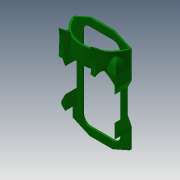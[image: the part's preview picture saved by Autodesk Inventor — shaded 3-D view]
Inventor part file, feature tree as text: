
AUTODESK INVENTOR PART (.ipt)
format: ipt  version: 2013 (Build 170138000, 138)  size: 726,016 bytes
history: native  units: mm
features: sketch x30, extrude x29, chamfer x3, fillet x2
ambient origin geometry x8: Origin, YZ Plane, XZ Plane, XY Plane, X Axis, Y Axis, Z Axis, Center Point
bodies: Solid1 (feature_tree)
feature tree (64):
  extrude  "Extrusion1"  Depth=4.0mm
  extrude  "Extrusion2"  Depth=4.0mm
  extrude  "Extrusion3"  Depth=4.0mm
  fillet  "Fillet1"  Radius=4.0mm
  extrude  "Extrusion4"  Depth=4.0mm
  extrude  "Extrusion5"  Depth=4.0mm
  extrude  "Extrusion6"  Depth=4.0mm
  sketch  "Sketch8"  dims[d13=4.0mm d14=4.0mm]
  extrude  "Extrusion7"  Depth=4.0mm
  extrude  "Extrusion8"  Depth=4.0mm
  extrude  "Extrusion9"  Depth=4.0mm
  extrude  "Extrusion10"  Depth=4.0mm
  extrude  "Extrusion11"  Depth=4.0mm
  extrude  "Extrusion12"  Depth=4.0mm
  extrude  "Extrusion13"  Depth=1.3mm TaperAngle=0.0deg
  extrude  "Extrusion14"  Depth=10.0mm
  extrude  "Extrusion15"  Depth=10.0mm
  extrude  "Extrusion16"  Depth=10.0mm
  extrude  "Extrusion17"  Depth=20.0mm
  extrude  "Extrusion18"  Depth=3.3mm TaperAngle=0.0deg
  extrude  "Extrusion19"  Depth=80.0mm
  extrude  "Extrusion20"  Depth=20.0mm TaperAngle=0.0deg
  chamfer  "Chamfer8"  Distance=30.0mm
  chamfer  "Chamfer9"  Distance=30.0mm
  chamfer  "Chamfer10"  Distance=35.0mm
  fillet  "Fillet6"  Radius=3.0mm
  extrude  "Extrusion21"  Depth=6.2mm TaperAngle=0.0deg
  extrude  "Extrusion22"  Depth=6.2mm TaperAngle=0.0deg
  extrude  "Extrusion23"  Depth=83.5mm
  extrude  "Extrusion24"  Depth=35.0mm TaperAngle=0.0deg
  extrude  "Extrusion25"  Depth=3.0mm
  extrude  "Extrusion26"  Depth=35.0mm TaperAngle=0.0deg
  extrude  "Extrusion27"  Depth=12.85mm TaperAngle=45.0deg
  extrude  "Extrusion28"  Depth=10.0mm TaperAngle=45.0deg
  extrude  "Extrusion29"  Depth=8.0mm
  sketch  "Sketch1"  dims[d0=4.0mm d1=4.0mm]
  sketch  "Sketch2"  dims[d2=4.0mm d3=4.0mm]
  sketch  "Sketch3"  dims[d4=4.0mm d5=4.0mm d6=4.0mm]
  sketch  "Sketch5"  dims[d7=4.0mm d8=4.0mm]
  sketch  "Sketch6"  dims[d9=4.0mm d10=4.0mm]
  sketch  "Sketch7"  dims[d11=4.0mm d12=4.0mm]
  sketch  "Sketch9"  dims[d15=4.0mm d16=4.0mm]
  sketch  "Sketch10"  dims[d17=4.0mm d18=4.0mm]
  sketch  "Sketch11"  dims[d19=4.0mm d20=4.0mm]
  sketch  "Sketch12"  dims[d21=4.0mm d22=4.0mm]
  sketch  "Sketch13"  dims[d23=4.0mm d24=4.0mm]
  sketch  "Sketch14"  dims[d25=2.0mm d26=0.0mm d27=1.3mm d28=0.0mm]
  sketch  "Sketch15"  dims[d29=10.0mm d30=10.0mm]
  sketch  "Sketch16"  dims[d31=10.0mm d32=10.0mm]
  sketch  "Sketch17"  dims[d33=10.0mm d34=10.0mm]
  sketch  "Sketch18"  dims[d35=3.3mm d36=0.0mm d37=20.0mm]
  sketch  "Sketch19"  dims[d38=3.0mm d39=0.0mm d40=3.3mm d41=0.0mm]
  sketch  "Sketch20"  dims[d42=1.7mm d43=0.0mm d46=80.0mm]
  sketch  "Sketch21"  dims[d47=65.0mm d48=0.0mm d49=20.0mm d50=0.0mm]
  sketch  "Sketch22"  dims[d51=53.0mm d52=30.0mm d53=0.0mm d54=30.0mm d55=0.0mm d56=35.0mm d57=0.0mm d58=3.0mm]
  sketch  "Sketch23"  dims[d59=3.0mm d61=6.2mm d62=0.0mm]
  sketch  "Sketch24"  dims[d63=35.0mm d64=0.0mm d84=6.2mm d85=0.0mm]
  sketch  "Sketch25"  dims[d86=30.0mm d87=0.0mm d88=83.5mm]
  sketch  "Sketch26"  dims[d89=30.0mm d90=0.0mm d91=35.0mm d92=0.0mm]
  sketch  "Sketch27"  dims[d93=3.0mm d94=3.0mm]
  sketch  "Sketch28"  dims[d95=5.0mm d96=0.0mm d97=35.0mm d98=0.0mm]
  sketch  "Sketch29"  dims[d99=1.2mm d100=0.0mm d107=12.85mm d108=2.0mm d109=45.0deg]
  sketch  "Sketch30"  dims[d110=10.0mm d111=2.0mm d112=45.0deg d113=10.0mm d114=2.0mm d115=45.0deg]
  sketch  "Sketch31"  dims[d116=21.0mm d117=8.0mm d119=30.0mm d120=0.0mm d121=82.6mm d123=5.0mm d130=7.0mm d131=28.0mm d132=45.0mm d133=0.0mm d134=20.0mm d135=0.0mm d136=12.0mm d137=0.0mm d138=12.0mm d139=0.0mm d142=12.0mm d143=0.0mm d144=12.0mm d145=0.0mm d146=20.0mm d147=6.0mm d148=0.0mm d149=6.0mm d150=0.0mm]
